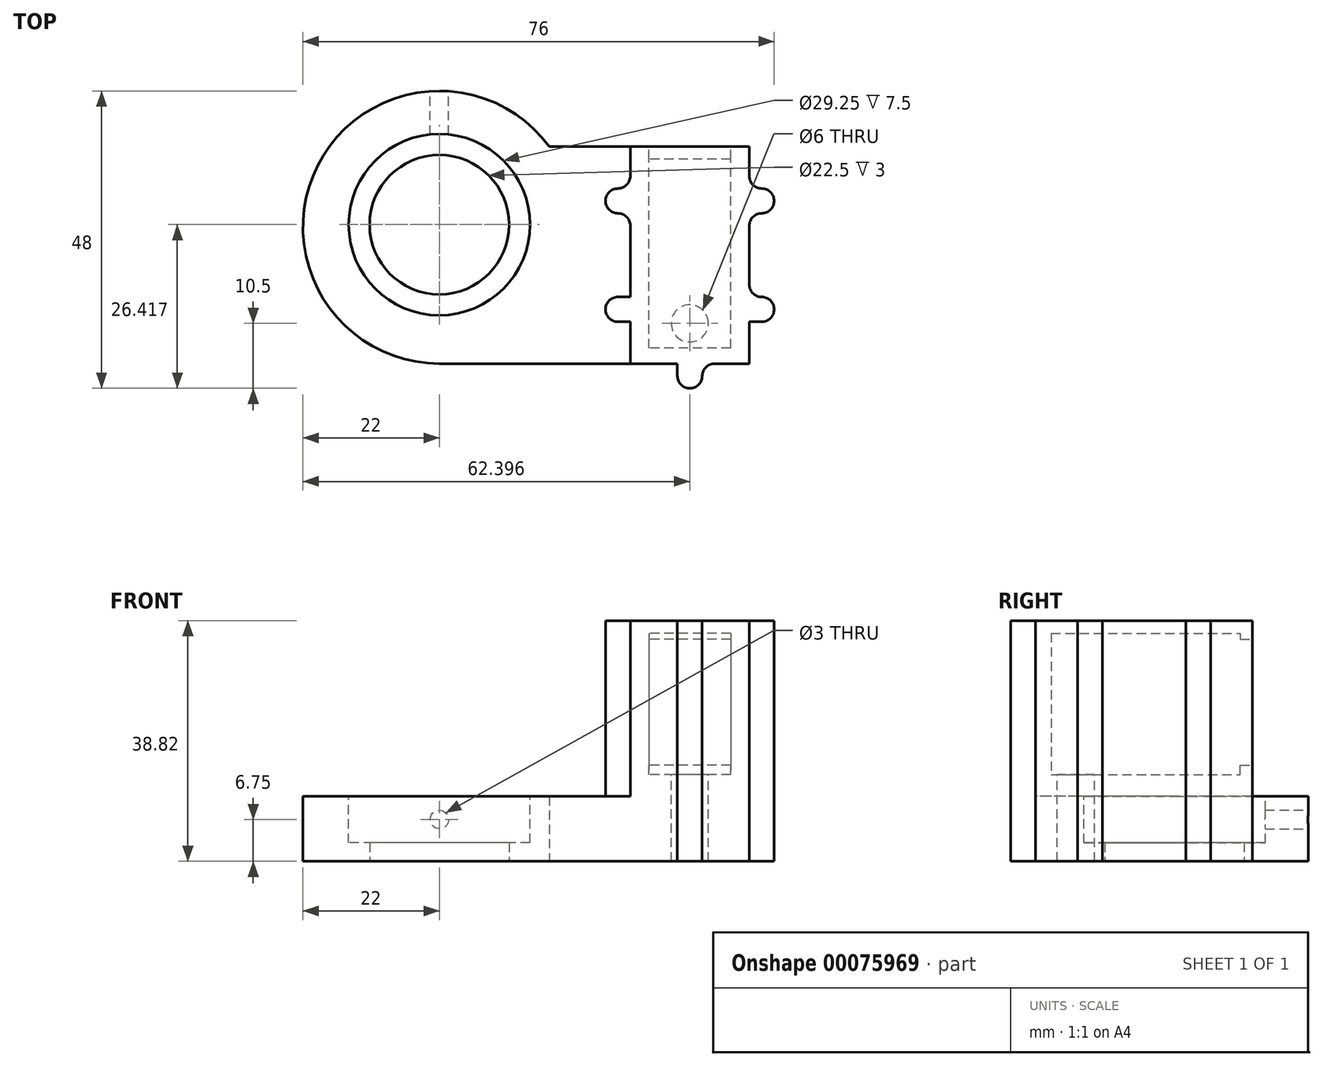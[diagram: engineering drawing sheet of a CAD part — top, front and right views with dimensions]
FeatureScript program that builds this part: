
annotation { "Feature Type Name" : "Feature", "Feature Type Description" : "" }
export const myFeature = defineFeature(function(context is Context, id is Id, definition is map)
    precondition{}
    {
        {
            var Q0;
            Q0=qCreatedBy(makeId("Top.planeOp"),FACE);
            var sketch = newSketch(context, id + "F0", { "sketchPlane" : qUnion([Q0])});
            skCircle(sketch, "E0", {"center": v(0, 0.42) * mm, "radius": 11.25 * mm});
            skCircle(sketch, "E1", {"center": v(0, 0) * mm, "radius": 22 * mm});
            skSolve(sketch);
        }
        {
            var Q0;
            Q0=makeQuery(id+"F0.imprint","IMPRINT",FACE,{"disambiguationData":[TD([[makeQuery(id+"F0.imprint","IMPRINT",EDGE,{"derivedFrom":sQuery(id+"F0.wireOp",EDGE,"E0")}),-1.0]])]});
            extrude(context, id + "F1", {"entities" : qUnion([Q0]), "depth" : 10.5 * mm});
        }
        {
            var Q0;
            Q0=qCreatedBy(makeId("Top.planeOp"),FACE);
            var sketch = newSketch(context, id + "F2", { "sketchPlane" : qUnion([Q0])});
            skLineSegment(sketch, "E2", {"start": v(50, -22) * mm, "end": v(50, 13) * mm});
            skLineSegment(sketch, "E3", {"start": v(50, 13) * mm, "end": v(17.75, 13) * mm});
            skArc(sketch, "E4", {"start": v(0, -22) * mm, "mid": v(19.62, -9.95) * mm, "end": v(17.75, 13) * mm});
            skLineSegment(sketch, "E5", {"start": v(0, -22) * mm, "end": v(50, -22) * mm});
            skSolve(sketch);
        }
        {
            var Q0;
            Q0 = qSketchRegion(id + "F2", true);
            extrude(context, id + "F3", {"entities" : qUnion([Q0]), "operationType" : NewBodyOperationType.ADD, "depth" : 38.82 * mm});
        }
        {
            var Q0;
            Q0=makeQuery(id+"FZENi5TM40lAH7P_1.boolean.opBoolean","MERGE",FACE,{"derivedFrom":[makeQuery(id+"F1.opExtrude","CAP_FACE",FACE,{"disambiguationData":[OSD([sQuery(id+"F0.wireOp",EDGE,"E0"),sQuery(id+"F0.wireOp",EDGE,"E1")])],"isStart":false}),makeQuery(id+"FZENi5TM40lAH7P_1.opExtrude","SWEPT_FACE",FACE,{"disambiguationData":[OSD([sQuery(id+"FEa8PfG2waAYveU_1.wireOp",EDGE,"Q2r3smx6-8iro-VQHo-lUVp-GLQQrc060Jvu")])]})]});
            var sketch = newSketch(context, id + "F4", { "sketchPlane" : qUnion([Q0])});
            skCircle(sketch, "E6", {"center": v(0, 0.42) * mm, "radius": 11.13 * mm});
            skCircle(sketch, "E7", {"center": v(0, 0.42) * mm, "radius": 14.62 * mm});
            skSolve(sketch);
        }
        {
            var Q0;
            Q0 = qSketchRegion(id + "F4", true);
            extrude(context, id + "F5", {"entities" : qUnion([Q0]), "operationType" : NewBodyOperationType.REMOVE, "oppositeDirection" : true, "depth" : 7.5 * mm});
        }
        {
            var Q0;
            Q0=qCreatedBy(makeId("Front.planeOp"),FACE);
            cPlane(context, id + "F6", {"entities" : qUnion([Q0]), "cplaneType" : CPlaneType.OFFSET, "offset" : 22 * mm, "oppositeDirection" : true, "width" : 150 * mm, "height" : 150 * mm});
        }
        {
            var Q0;
            Q0=qCreatedBy(id+"F6.planeOp",FACE);
            var sketch = newSketch(context, id + "F7", { "sketchPlane" : qUnion([Q0])});
            skPoint(sketch, "E8.orphan", {"position": v(0, 0) * mm});
            skLineSegment(sketch, "E9", {"start": v(0, 3) * mm, "end": v(0, 10.5) * mm, "construction": true});
            skCircle(sketch, "E10", {"center": v(0, 6.75) * mm, "radius": 1.5 * mm});
            skSolve(sketch);
        }
        {
            var Q0;
            Q0=makeQuery(id+"F3.opExtrude","SWEPT_FACE",FACE,{"disambiguationData":[OSD([sQuery(id+"F2.wireOp",EDGE,"E3")])]});
            var sketch = newSketch(context, id + "F8", { "sketchPlane" : qUnion([Q0])});
            skPoint(sketch, "E11.endSnap0", {"position": v(-32.75, 0) * mm});
            skPoint(sketch, "E12.middle", {"position": v(-36.75, 19.41) * mm});
            skLineSegment(sketch, "E13", {"start": v(-40.4, 35.82) * mm, "end": v(-40.4, 25.66) * mm, "construction": true});
            skLineSegment(sketch, "E14.bottom", {"start": v(-47, 35.82) * mm, "end": v(-33.8, 35.82) * mm});
            skLineSegment(sketch, "E14.top", {"start": v(-47, 15.5) * mm, "end": v(-33.8, 15.5) * mm});
            skLineSegment(sketch, "E14.left", {"start": v(-47, 35.82) * mm, "end": v(-47, 15.5) * mm});
            skLineSegment(sketch, "E14.right", {"start": v(-33.8, 35.82) * mm, "end": v(-33.8, 15.5) * mm});
            skPoint(sketch, "E14.middle", {"position": v(-40.4, 25.66) * mm});
            skLineSegment(sketch, "E15", {"start": v(-33.87, 38.82) * mm, "end": v(-33.87, 35.82) * mm, "construction": true});
            skLineSegment(sketch, "E16", {"start": v(-47, 35.82) * mm, "end": v(-50, 35.82) * mm, "construction": true});
            skSolve(sketch);
        }
        {
            var Q0;
            Q0 = qSketchRegion(id + "F8", true);
            extrude(context, id + "F9", {"entities" : qUnion([Q0]), "operationType" : NewBodyOperationType.REMOVE, "oppositeDirection" : true, "depth" : 32.5 * mm});
        }
        {
            var Q0;
            Q0=makeQuery(id+"F9.boolean.opBoolean","COPY",FACE,{"derivedFrom":makeQuery(id+"F9.opExtrude","SWEPT_FACE",FACE,{"disambiguationData":[OSD([sQuery(id+"F8.wireOp",EDGE,"E14.top")])]})});
            var sketch = newSketch(context, id + "F10", { "sketchPlane" : qUnion([Q0])});
            skLineSegment(sketch, "E17", {"start": v(40.4, -19.5) * mm, "end": v(40.4, -15.5) * mm, "construction": true});
            skCircle(sketch, "E18", {"center": v(40.4, -15.5) * mm, "radius": 3 * mm});
            skSolve(sketch);
        }
        {
            var Q0;
            Q0 = qSketchRegion(id + "F10", true);
            extrude(context, id + "F11", {"entities" : qUnion([Q0]), "operationType" : NewBodyOperationType.REMOVE, "endBound" : BoundingType.UP_TO_NEXT, "oppositeDirection" : true, "depth" : 25 * mm});
        }
        {
            var Q0;
            Q0=makeQuery(id+"F9.boolean.opBoolean","COPY",FACE,{"derivedFrom":makeQuery(id+"F9.opExtrude","SWEPT_FACE",FACE,{"disambiguationData":[OSD([sQuery(id+"F8.wireOp",EDGE,"E14.top")])]})});
            var sketch = newSketch(context, id + "F12", { "sketchPlane" : qUnion([Q0])});
            skLineSegment(sketch, "E19", {"start": v(33.8, -19.5) * mm, "end": v(47, -19.5) * mm});
            skLineSegment(sketch, "E20", {"start": v(47, -19.5) * mm, "end": v(47, 11) * mm});
            skLineSegment(sketch, "E21", {"start": v(47, 11) * mm, "end": v(33.8, 11) * mm});
            skLineSegment(sketch, "E22", {"start": v(33.8, 11) * mm, "end": v(33.8, -19.5) * mm});
            skSolve(sketch);
        }
        {
            var Q0;
            Q0 = qSketchRegion(id + "F12", true);
            extrude(context, id + "F13", {"entities" : qUnion([Q0]), "operationType" : NewBodyOperationType.REMOVE, "oppositeDirection" : true, "depth" : 1.5 * mm});
        }
        {
            var Q0;
            Q0=makeQuery(id+"F9.boolean.opBoolean","COPY",FACE,{"derivedFrom":makeQuery(id+"F9.opExtrude","SWEPT_FACE",FACE,{"disambiguationData":[OSD([sQuery(id+"F8.wireOp",EDGE,"E14.bottom")])]})});
            var sketch = newSketch(context, id + "F14", { "sketchPlane" : qUnion([Q0])});
            skLineSegment(sketch, "E23", {"start": v(33.8, 19.5) * mm, "end": v(47, 19.5) * mm});
            skLineSegment(sketch, "E24", {"start": v(47, 19.5) * mm, "end": v(47, -11) * mm});
            skLineSegment(sketch, "E25", {"start": v(47, -11) * mm, "end": v(33.8, -11) * mm});
            skLineSegment(sketch, "E26", {"start": v(33.8, -11) * mm, "end": v(33.8, 19.5) * mm});
            skSolve(sketch);
        }
        {
            var Q0;
            Q0 = qSketchRegion(id + "F14", true);
            extrude(context, id + "F15", {"entities" : qUnion([Q0]), "operationType" : NewBodyOperationType.REMOVE, "oppositeDirection" : true, "depth" : 1 * mm});
        }
        {
            var Q0;
            Q0=makeQuery(id+"F3.opExtrude","SWEPT_FACE",FACE,{"disambiguationData":[OSD([sQuery(id+"F2.wireOp",EDGE,"E5")])]});
            var sketch = newSketch(context, id + "F16", { "sketchPlane" : qUnion([Q0])});
            skLineSegment(sketch, "E27.bottom", {"start": v(0, 38.82) * mm, "end": v(30.8, 38.82) * mm});
            skLineSegment(sketch, "E27.top", {"start": v(0, 10.5) * mm, "end": v(30.8, 10.5) * mm});
            skLineSegment(sketch, "E27.left", {"start": v(0, 38.82) * mm, "end": v(0, 10.5) * mm});
            skLineSegment(sketch, "E27.right", {"start": v(30.8, 38.82) * mm, "end": v(30.8, 10.5) * mm});
            skSolve(sketch);
        }
        {
            var Q0;
            Q0 = qSketchRegion(id + "F16", true);
            extrude(context, id + "F17", {"entities" : qUnion([Q0]), "operationType" : NewBodyOperationType.REMOVE, "endBound" : BoundingType.THROUGH_ALL, "oppositeDirection" : true, "depth" : 25 * mm});
        }
        {
            var Q0;
            Q0=makeQuery(id+"F3.opExtrude","CAP_FACE",FACE,{"disambiguationData":[OSD([sQuery(id+"F2.wireOp",EDGE,"oOEIpuG3-JZhW-O0GC-rQoD-f2R3o1l9wmm3"),sQuery(id+"F2.wireOp",EDGE,"8okTQ8Sj-Ifpl-at7G-Ejs2-UwFY9ZqNEdEu"),sQuery(id+"F2.wireOp",EDGE,"E2"),sQuery(id+"F2.wireOp",EDGE,"E3")])],"isStart":false});
            var sketch = newSketch(context, id + "F18", { "sketchPlane" : qUnion([Q0])});
            skLineSegment(sketch, "E28", {"start": v(50, -4.5) * mm, "end": v(50, 13) * mm, "construction": true});
            skLineSegment(sketch, "E29", {"start": v(50, -4.5) * mm, "end": v(30.8, -4.5) * mm, "construction": true});
            skLineSegment(sketch, "E30", {"start": v(50, 4.25) * mm, "end": v(52, 4.25) * mm, "construction": true});
            skLineSegment(sketch, "E31.bottom", {"start": v(50, 2.25) * mm, "end": v(54, 2.25) * mm});
            skLineSegment(sketch, "E31.top", {"start": v(50, 6.25) * mm, "end": v(54, 6.25) * mm});
            skLineSegment(sketch, "E31.left", {"start": v(50, 2.25) * mm, "end": v(50, 6.25) * mm});
            skLineSegment(sketch, "E31.right", {"start": v(54, 2.25) * mm, "end": v(54, 6.25) * mm});
            skPoint(sketch, "E31.middle", {"position": v(52, 4.25) * mm});
            skLineSegment(sketch, "E32.MirrorCS", {"start": v(54, -11.25) * mm, "end": v(54, -15.25) * mm});
            skLineSegment(sketch, "E33.MirrorCS", {"start": v(50, -15.25) * mm, "end": v(54, -15.25) * mm});
            skLineSegment(sketch, "E34.MirrorCS", {"start": v(50, -11.25) * mm, "end": v(54, -11.25) * mm});
            skLineSegment(sketch, "E35.MirrorCS", {"start": v(50, -11.25) * mm, "end": v(50, -15.25) * mm});
            skLineSegment(sketch, "E36", {"start": v(40.4, -22) * mm, "end": v(40.4, -4.5) * mm, "construction": true});
            skLineSegment(sketch, "E37.MirrorCS", {"start": v(30.8, -11.25) * mm, "end": v(30.8, -15.25) * mm});
            skLineSegment(sketch, "E38.MirrorCS", {"start": v(30.8, -11.25) * mm, "end": v(26.8, -11.25) * mm});
            skLineSegment(sketch, "E39.MirrorCS", {"start": v(26.8, -11.25) * mm, "end": v(26.8, -15.25) * mm});
            skLineSegment(sketch, "E40.MirrorCS", {"start": v(30.8, -15.25) * mm, "end": v(26.8, -15.25) * mm});
            skLineSegment(sketch, "E41.MirrorCS", {"start": v(30.8, 2.25) * mm, "end": v(26.8, 2.25) * mm});
            skLineSegment(sketch, "E42.MirrorCS", {"start": v(30.8, 2.25) * mm, "end": v(30.8, 6.25) * mm});
            skLineSegment(sketch, "E43.MirrorCS", {"start": v(30.8, 6.25) * mm, "end": v(26.8, 6.25) * mm});
            skLineSegment(sketch, "E44.MirrorCS", {"start": v(26.8, 2.25) * mm, "end": v(26.8, 6.25) * mm});
            skLineSegment(sketch, "E45", {"start": v(40.4, -22) * mm, "end": v(40.4, -24) * mm});
            skLineSegment(sketch, "E46.bottom", {"start": v(38.4, -22) * mm, "end": v(42.4, -22) * mm});
            skLineSegment(sketch, "E46.top", {"start": v(38.4, -26) * mm, "end": v(42.4, -26) * mm});
            skLineSegment(sketch, "E46.left", {"start": v(38.4, -22) * mm, "end": v(38.4, -26) * mm});
            skLineSegment(sketch, "E46.right", {"start": v(42.4, -22) * mm, "end": v(42.4, -26) * mm});
            skPoint(sketch, "E46.middle", {"position": v(40.4, -24) * mm});
            skSolve(sketch);
        }
        {
            var Q0;
            Q0 = qSketchRegion(id + "F18", true);
            var Q1;
            Q1=makeQuery(id+"FZENi5TM40lAH7P_1.boolean.opBoolean","MERGE",FACE,{"derivedFrom":[makeQuery(id+"F1.opExtrude","CAP_FACE",FACE,{"disambiguationData":[OSD([sQuery(id+"F0.wireOp",EDGE,"E0"),sQuery(id+"F0.wireOp",EDGE,"E1")])],"isStart":false}),makeQuery(id+"FZENi5TM40lAH7P_1.opExtrude","SWEPT_FACE",FACE,{"disambiguationData":[OSD([sQuery(id+"FEa8PfG2waAYveU_1.wireOp",EDGE,"Q2r3smx6-8iro-VQHo-lUVp-GLQQrc060Jvu")])]})]});
            var Q2;
            Q2=makeQuery(id+"F3.boolean.opBoolean","MERGE",FACE,{"derivedFrom":[makeQuery(id+"F1.opExtrude","CAP_FACE",FACE,{"disambiguationData":[OSD([sQuery(id+"F0.wireOp",EDGE,"E0"),sQuery(id+"F0.wireOp",EDGE,"E1")])],"isStart":true}),makeQuery(id+"F3.opExtrude","CAP_FACE",FACE,{"disambiguationData":[OSD([sQuery(id+"F2.wireOp",EDGE,"oOEIpuG3-JZhW-O0GC-rQoD-f2R3o1l9wmm3"),sQuery(id+"F2.wireOp",EDGE,"8okTQ8Sj-Ifpl-at7G-Ejs2-UwFY9ZqNEdEu"),sQuery(id+"F2.wireOp",EDGE,"E2"),sQuery(id+"F2.wireOp",EDGE,"E3")])],"isStart":true})]});
            extrude(context, id + "F19", {"entities" : qUnion([Q0, Q1]), "operationType" : NewBodyOperationType.ADD, "endBound" : BoundingType.UP_TO_SURFACE, "oppositeDirection" : true, "endBoundEntityFace" : qUnion([Q2]), "depth" : 25 * mm});
        }
        {
            var Q0;
            Q0=makeQuery(id+"F19.opExtrude","SWEPT_EDGE",EDGE,{"disambiguationData":[OSD([sQuery(id+"F18.wireOp",EDGE,"E46.top"),sQuery(id+"F18.wireOp",EDGE,"E46.right")])]});
            var Q1;
            Q1=makeQuery(id+"F19.opExtrude","SWEPT_EDGE",EDGE,{"disambiguationData":[OSD([sQuery(id+"F18.wireOp",EDGE,"E46.top"),sQuery(id+"F18.wireOp",EDGE,"E46.left")])]});
            var Q2;
            Q2=makeQuery(id+"F19.opExtrude","SWEPT_EDGE",EDGE,{"disambiguationData":[OSD([sQuery(id+"F2.wireOp",EDGE,"8okTQ8Sj-Ifpl-at7G-Ejs2-UwFY9ZqNEdEu"),sQuery(id+"F18.wireOp",EDGE,"E46.bottom"),sQuery(id+"F18.wireOp",EDGE,"E46.right")])]});
            var Q3;
            Q3=makeQuery(id+"F19.opExtrude","SWEPT_EDGE",EDGE,{"disambiguationData":[OSD([sQuery(id+"F2.wireOp",EDGE,"E2"),sQuery(id+"F18.wireOp",EDGE,"E33.MirrorCS"),sQuery(id+"F18.wireOp",EDGE,"E35.MirrorCS")])]});
            var Q4;
            Q4=makeQuery(id+"F19.opExtrude","SWEPT_EDGE",EDGE,{"disambiguationData":[OSD([sQuery(id+"F18.wireOp",EDGE,"E32.MirrorCS"),sQuery(id+"F18.wireOp",EDGE,"E33.MirrorCS")])]});
            var Q5;
            Q5=makeQuery(id+"F19.opExtrude","SWEPT_EDGE",EDGE,{"disambiguationData":[OSD([sQuery(id+"F18.wireOp",EDGE,"E32.MirrorCS"),sQuery(id+"F18.wireOp",EDGE,"E34.MirrorCS")])]});
            var Q6;
            Q6=makeQuery(id+"F19.opExtrude","SWEPT_EDGE",EDGE,{"disambiguationData":[OSD([sQuery(id+"F2.wireOp",EDGE,"E2"),sQuery(id+"F18.wireOp",EDGE,"E31.bottom"),sQuery(id+"F18.wireOp",EDGE,"E31.left")])]});
            var Q7;
            Q7=makeQuery(id+"F19.opExtrude","SWEPT_EDGE",EDGE,{"disambiguationData":[OSD([sQuery(id+"F18.wireOp",EDGE,"E31.bottom"),sQuery(id+"F18.wireOp",EDGE,"E31.right")])]});
            var Q8;
            Q8=makeQuery(id+"F19.opExtrude","SWEPT_EDGE",EDGE,{"disambiguationData":[OSD([sQuery(id+"F18.wireOp",EDGE,"E31.top"),sQuery(id+"F18.wireOp",EDGE,"E31.right")])]});
            var Q9;
            Q9=makeQuery(id+"F19.opExtrude","SWEPT_EDGE",EDGE,{"disambiguationData":[OSD([sQuery(id+"F18.wireOp",EDGE,"E41.MirrorCS"),sQuery(id+"F18.wireOp",EDGE,"E44.MirrorCS")])]});
            var Q10;
            Q10=makeQuery(id+"F19.opExtrude","SWEPT_EDGE",EDGE,{"disambiguationData":[OSD([sQuery(id+"F18.wireOp",EDGE,"E39.MirrorCS"),sQuery(id+"F18.wireOp",EDGE,"E40.MirrorCS")])]});
            var Q11;
            Q11=makeQuery(id+"F19.opExtrude","SWEPT_EDGE",EDGE,{"disambiguationData":[OSD([sQuery(id+"F2.wireOp",EDGE,"E2"),sQuery(id+"F18.wireOp",EDGE,"E34.MirrorCS"),sQuery(id+"F18.wireOp",EDGE,"E35.MirrorCS")])]});
            var Q12;
            Q12=makeQuery(id+"F19.opExtrude","SWEPT_EDGE",EDGE,{"disambiguationData":[OSD([sQuery(id+"F2.wireOp",EDGE,"E2"),sQuery(id+"F18.wireOp",EDGE,"E31.top"),sQuery(id+"F18.wireOp",EDGE,"E31.left")])]});
            var Q13;
            Q13=makeQuery(id+"F19.opExtrude","SWEPT_EDGE",EDGE,{"disambiguationData":[OSD([sQuery(id+"F2.wireOp",EDGE,"8okTQ8Sj-Ifpl-at7G-Ejs2-UwFY9ZqNEdEu"),sQuery(id+"F18.wireOp",EDGE,"E46.bottom"),sQuery(id+"F18.wireOp",EDGE,"E46.left")])]});
            var Q14;
            Q14=makeQuery(id+"F19.opExtrude","SWEPT_EDGE",EDGE,{"disambiguationData":[OSD([sQuery(id+"F2.wireOp",EDGE,"8okTQ8Sj-Ifpl-at7G-Ejs2-UwFY9ZqNEdEu"),sQuery(id+"FEa8PfG2waAYveU_1.wireOp",EDGE,"ILBekNz5-4cCq-1ys0-y3Fu-rLsFxE4UrWBO"),sQuery(id+"FEa8PfG2waAYveU_1.wireOp",EDGE,"Ah70fClN-lh2n-Em30-fsup-SuxjUJYHkB6F"),sQuery(id+"F18.wireOp",EDGE,"E37.MirrorCS"),sQuery(id+"F18.wireOp",EDGE,"E40.MirrorCS")])]});
            var Q15;
            Q15=makeQuery(id+"F19.opExtrude","SWEPT_EDGE",EDGE,{"disambiguationData":[OSD([sQuery(id+"F2.wireOp",EDGE,"8okTQ8Sj-Ifpl-at7G-Ejs2-UwFY9ZqNEdEu"),sQuery(id+"FEa8PfG2waAYveU_1.wireOp",EDGE,"ILBekNz5-4cCq-1ys0-y3Fu-rLsFxE4UrWBO"),sQuery(id+"FEa8PfG2waAYveU_1.wireOp",EDGE,"Ah70fClN-lh2n-Em30-fsup-SuxjUJYHkB6F"),sQuery(id+"F18.wireOp",EDGE,"E41.MirrorCS"),sQuery(id+"F18.wireOp",EDGE,"E42.MirrorCS")])]});
            var Q16;
            Q16=makeQuery(id+"F19.opExtrude","SWEPT_EDGE",EDGE,{"disambiguationData":[OSD([sQuery(id+"F18.wireOp",EDGE,"E38.MirrorCS"),sQuery(id+"F18.wireOp",EDGE,"E39.MirrorCS")])]});
            var Q17;
            Q17=makeQuery(id+"F19.opExtrude","SWEPT_EDGE",EDGE,{"disambiguationData":[OSD([sQuery(id+"F18.wireOp",EDGE,"E43.MirrorCS"),sQuery(id+"F18.wireOp",EDGE,"E44.MirrorCS")])]});
            var Q18;
            Q18=makeQuery(id+"F19.opExtrude","SWEPT_EDGE",EDGE,{"disambiguationData":[OSD([sQuery(id+"F2.wireOp",EDGE,"8okTQ8Sj-Ifpl-at7G-Ejs2-UwFY9ZqNEdEu"),sQuery(id+"FEa8PfG2waAYveU_1.wireOp",EDGE,"ILBekNz5-4cCq-1ys0-y3Fu-rLsFxE4UrWBO"),sQuery(id+"FEa8PfG2waAYveU_1.wireOp",EDGE,"Ah70fClN-lh2n-Em30-fsup-SuxjUJYHkB6F"),sQuery(id+"F18.wireOp",EDGE,"E42.MirrorCS"),sQuery(id+"F18.wireOp",EDGE,"E43.MirrorCS")])]});
            fillet(context, id + "F20", {"entities" : qUnion([Q0, Q1, Q2, Q3, Q4, Q5, Q6, Q7, Q8, Q9, Q10, Q11, Q12, Q13, Q14, Q15, Q16, Q17, Q18]), "radius" : 2 * mm, "tangentPropagation" : true, "allowEdgeOverflow" : false});
        }
        {
            var Q0;
            Q0=makeQuery(id+"F7.imprint","IMPRINT",FACE,{"disambiguationData":[TD([[makeQuery(id+"F7.imprint","IMPRINT",EDGE,{"derivedFrom":sQuery(id+"F7.wireOp",EDGE,"E10")}),1.0]])]});
            var Q1;
            Q1=sQuery(id+"F7.wireOp",EDGE,"E10");
            extrude(context, id + "F21", {"entities" : qUnion([Q0]), "operationType" : NewBodyOperationType.REMOVE, "surfaceEntities" : qUnion([Q1]), "depth" : 10 * mm});
        }
    });
